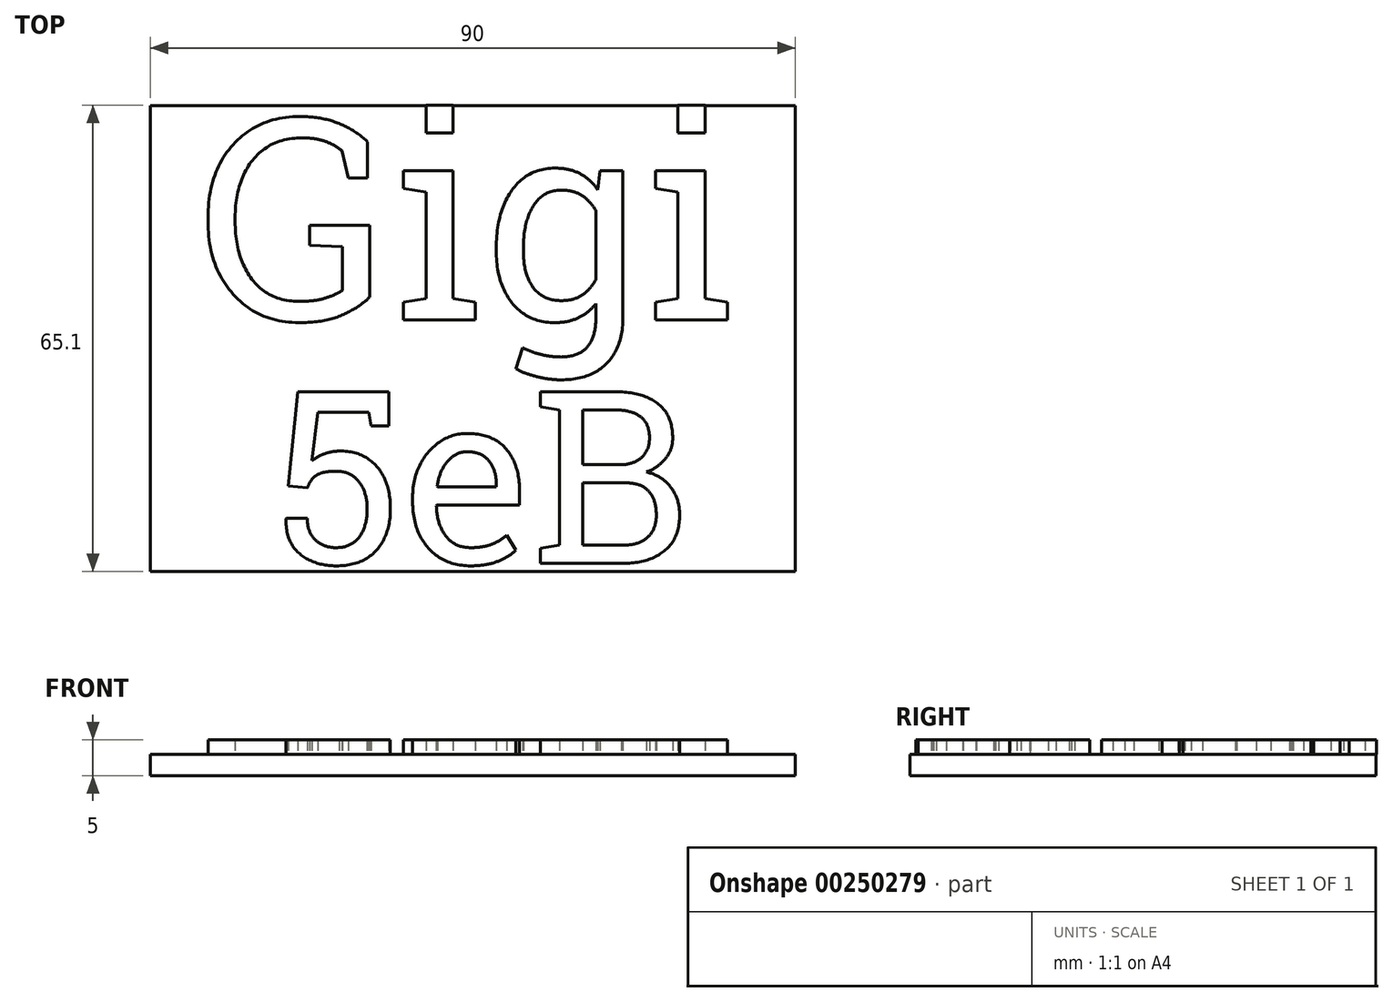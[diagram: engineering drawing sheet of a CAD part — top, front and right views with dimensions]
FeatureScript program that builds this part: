
annotation { "Feature Type Name" : "Feature", "Feature Type Description" : "" }
export const myFeature = defineFeature(function(context is Context, id is Id, definition is map)
    precondition{}
    {
        {
            var Q0;
            Q0=qCreatedBy(makeId("Top.planeOp"),FACE);
            var sketch = newSketch(context, id + "F0", { "sketchPlane" : qUnion([Q0])});
            skLineSegment(sketch, "E0.bottom", {"start": v(0, 0) * mm, "end": v(90, 0) * mm});
            skLineSegment(sketch, "E0.top", {"start": v(0, -65) * mm, "end": v(90, -65) * mm});
            skLineSegment(sketch, "E0.left", {"start": v(0, 0) * mm, "end": v(0, -65) * mm});
            skLineSegment(sketch, "E0.right", {"start": v(90, 0) * mm, "end": v(90, -65) * mm});
            skSolve(sketch);
        }
        {
            var Q0;
            Q0=makeQuery(id+"F0.imprint","IMPRINT",FACE,{"disambiguationData":[TD([[makeQuery(id+"F0.imprint","IMPRINT",EDGE,{"derivedFrom":sQuery(id+"F0.wireOp",EDGE,"E0.bottom")}),-1.0]])]});
            extrude(context, id + "F1", {"entities" : qUnion([Q0]), "depth" : 3 * mm});
        }
        {
            var Q0;
            Q0=makeQuery(id+"F1.opExtrude","CAP_FACE",FACE,{"disambiguationData":[OSD([sQuery(id+"F0.wireOp",EDGE,"E0.bottom"),sQuery(id+"F0.wireOp",EDGE,"E0.top"),sQuery(id+"F0.wireOp",EDGE,"E0.left"),sQuery(id+"F0.wireOp",EDGE,"E0.right")])],"isStart":false});
            var sketch = newSketch(context, id + "F2", { "sketchPlane" : qUnion([Q0])});
            skText(sketch, "E1", { "text": "Gigi\n\n", "fontName": "RobotoSlab-Regular.ttf"});
            skText(sketch, "E2", { "text": "5eB", "fontName": "RobotoSlab-Regular.ttf"});
            const initialGuessF2  = {"E1": [0.007, -0.02985, 1, 0, 0.02831], "E2": [0.01735, -0.06386, 1, 0, 0.02426]};
            skSetInitialGuess(sketch, initialGuessF2);
            skSolve(sketch);
        }
        {
            var Q0;
            Q0 = qSketchRegion(id + "F2", true);
            extrude(context, id + "F3", {"entities" : qUnion([Q0]), "operationType" : NewBodyOperationType.ADD, "depth" : 2 * mm});
        }
    });
